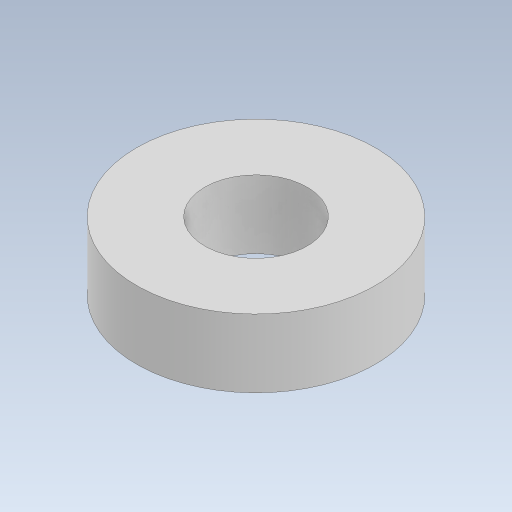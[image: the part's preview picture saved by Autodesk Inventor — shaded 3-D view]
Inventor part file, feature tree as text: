
AUTODESK INVENTOR PART (.ipt)
format: ipt  version: 2023.5 (Build 275446000, 446)  size: 248,320 bytes
history: native  units: mm
features: extrude x1, sketch x1
ambient origin geometry x8: Origin, YZ Plane, XZ Plane, XY Plane, X Axis, Y Axis, Z Axis, Center Point
bodies: Solid1 (feature_tree)
feature tree (2):
  extrude  "Extrusion1"  Depth=2.0mm
  sketch  "Sketch1"  dims[d0=3.0mm d1=7.0mm d2=2.0mm d3=0.0mm]
